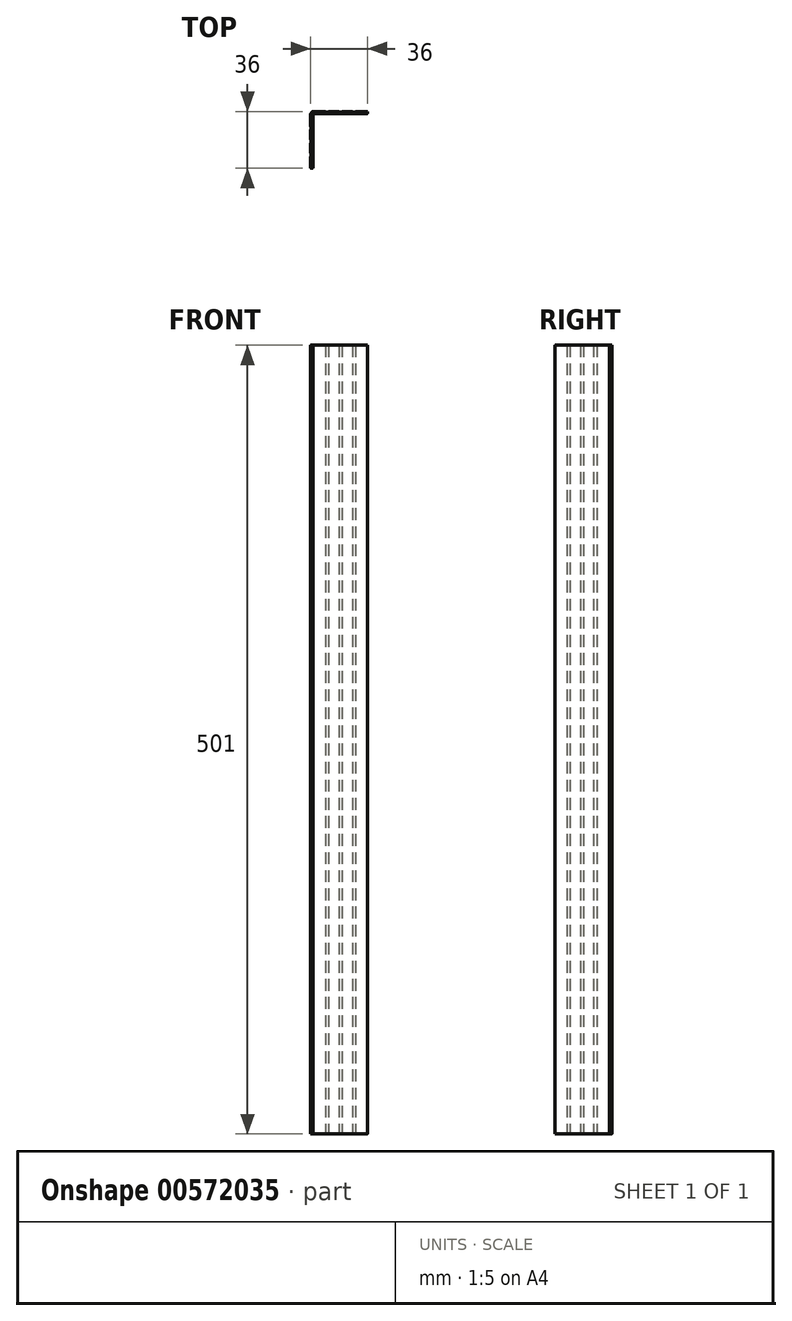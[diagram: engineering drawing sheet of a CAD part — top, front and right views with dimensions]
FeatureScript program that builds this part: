
annotation { "Feature Type Name" : "Feature", "Feature Type Description" : "" }
export const myFeature = defineFeature(function(context is Context, id is Id, definition is map)
    precondition{}
    {
        {
            var Q0;
            Q0=qCreatedBy(makeId("Top.planeOp"),FACE);
            var sketch = newSketch(context, id + "F0", { "sketchPlane" : qUnion([Q0])});
            skLineSegment(sketch, "E0", {"start": v(0, 0) * mm, "end": v(0, 7.5) * mm});
            skPoint(sketch, "E1.visualSharp", {"position": v(0, 36) * mm});
            skArc(sketch, "E1.filletArc", {"start": v(0.59, 35.41) * mm, "mid": v(0.15, 34.77) * mm, "end": v(0, 34) * mm});
            skLineSegment(sketch, "E2.1", {"start": v(1.5, 0) * mm, "end": v(1.5, 33.5) * mm});
            skLineSegment(sketch, "E3", {"start": v(1.5, 0) * mm, "end": v(0, 0) * mm});
            skPoint(sketch, "E4.visualSharp", {"position": v(1.5, 34.5) * mm});
            skArc(sketch, "E4.filletArc", {"start": v(1.8, 34.2) * mm, "mid": v(1.58, 33.88) * mm, "end": v(1.5, 33.5) * mm});
            skLineSegment(sketch, "E5.bottom", {"start": v(0, 18) * mm, "end": v(0.25, 18) * mm});
            skLineSegment(sketch, "E5.top", {"start": v(0, 16) * mm, "end": v(0.25, 16) * mm});
            skLineSegment(sketch, "E5.right", {"start": v(0.25, 18) * mm, "end": v(0.25, 16) * mm});
            skPoint(sketch, "E5.middle", {"position": v(0, 17) * mm});
            skLineSegment(sketch, "E6", {"start": v(0, 0) * mm, "end": v(-1.84, 0) * mm, "construction": true});
            skLineSegment(sketch, "E7", {"start": v(-1.84, 0) * mm, "end": v(-1.84, 17) * mm, "construction": true});
            skPoint(sketch, "E7.endSnap0", {"position": v(-0.25, 17) * mm});
            skLineSegment(sketch, "E8", {"start": v(-1.84, 8.5) * mm, "end": v(0, 8.5) * mm, "construction": true});
            skLineSegment(sketch, "E9.bottom", {"start": v(0.25, 9.5) * mm, "end": v(0, 9.5) * mm});
            skLineSegment(sketch, "E9.top", {"start": v(0.25, 7.5) * mm, "end": v(0, 7.5) * mm});
            skLineSegment(sketch, "E9.left", {"start": v(0.25, 9.5) * mm, "end": v(0.25, 7.5) * mm});
            skPoint(sketch, "E9.middle", {"position": v(0, 8.5) * mm});
            skLineSegment(sketch, "E10", {"start": v(-1.84, 17) * mm, "end": v(-1.84, 34) * mm, "construction": true});
            skLineSegment(sketch, "E11", {"start": v(-1.84, 25.5) * mm, "end": v(0, 25.5) * mm, "construction": true});
            skLineSegment(sketch, "E12.bottom", {"start": v(0.25, 26.5) * mm, "end": v(0, 26.5) * mm});
            skLineSegment(sketch, "E12.top", {"start": v(0.25, 24.5) * mm, "end": v(0, 24.5) * mm});
            skLineSegment(sketch, "E12.left", {"start": v(0.25, 26.5) * mm, "end": v(0.25, 24.5) * mm});
            skPoint(sketch, "E12.middle", {"position": v(0, 25.5) * mm});
            skPoint(sketch, "E13.end.orphan", {"position": v(36, 36) * mm});
            skLineSegment(sketch, "E14.trimOffspring", {"start": v(0, 9.5) * mm, "end": v(0, 16) * mm});
            skPoint(sketch, "E15.orphan", {"position": v(-0.25, 9.5) * mm});
            skPoint(sketch, "E16.orphan", {"position": v(-0.25, 7.5) * mm});
            skPoint(sketch, "E17.orphan", {"position": v(-0.25, 16) * mm});
            skLineSegment(sketch, "E18.trimOffspring", {"start": v(0, 18) * mm, "end": v(0, 24.5) * mm});
            skPoint(sketch, "E19.orphan", {"position": v(-0.25, 18) * mm});
            skLineSegment(sketch, "E20.trimOffspring", {"start": v(0, 26.5) * mm, "end": v(0, 34) * mm});
            skPoint(sketch, "E21.orphan", {"position": v(-0.25, 24.5) * mm});
            skPoint(sketch, "E22.orphan", {"position": v(-0.25, 26.5) * mm});
            skLineSegment(sketch, "E23.MirrorCS", {"start": v(11.5, 35.75) * mm, "end": v(11.5, 36) * mm});
            skLineSegment(sketch, "E24.MirrorCS", {"start": v(26.5, 35.75) * mm, "end": v(28.5, 35.75) * mm});
            skLineSegment(sketch, "E25.MirrorCS", {"start": v(28.5, 35.75) * mm, "end": v(28.5, 36) * mm});
            skLineSegment(sketch, "E26.MirrorCS", {"start": v(9.5, 35.75) * mm, "end": v(11.5, 35.75) * mm});
            skLineSegment(sketch, "E27.MirrorCS", {"start": v(9.5, 35.75) * mm, "end": v(9.5, 36) * mm});
            skLineSegment(sketch, "E28.MirrorCS", {"start": v(20, 36) * mm, "end": v(20, 35.75) * mm});
            skLineSegment(sketch, "E29.MirrorCS", {"start": v(26.5, 35.75) * mm, "end": v(26.5, 36) * mm});
            skLineSegment(sketch, "E30.MirrorCS", {"start": v(18, 35.75) * mm, "end": v(20, 35.75) * mm});
            skLineSegment(sketch, "E31.MirrorCS", {"start": v(18, 36) * mm, "end": v(18, 35.75) * mm});
            skArc(sketch, "E32.MirrorCS", {"start": v(1.8, 34.2) * mm, "mid": v(2.12, 34.42) * mm, "end": v(2.5, 34.5) * mm});
            skLineSegment(sketch, "E33.MirrorCS", {"start": v(36, 34.5) * mm, "end": v(36, 36) * mm});
            skArc(sketch, "E34.MirrorCS", {"start": v(0.59, 35.41) * mm, "mid": v(1.23, 35.85) * mm, "end": v(2, 36) * mm});
            skLineSegment(sketch, "E35.MirrorCS", {"start": v(10.5, 37.84) * mm, "end": v(10.5, 36) * mm, "construction": true});
            skLineSegment(sketch, "E36.MirrorCS", {"start": v(36, 36) * mm, "end": v(36, 37.84) * mm, "construction": true});
            skPoint(sketch, "E37.MirrorP", {"position": v(19, 36.25) * mm});
            skLineSegment(sketch, "E38.MirrorCS", {"start": v(27.5, 37.84) * mm, "end": v(27.5, 36) * mm, "construction": true});
            skPoint(sketch, "E39.MirrorP", {"position": v(19, 36) * mm});
            skLineSegment(sketch, "E40.MirrorCS", {"start": v(36, 34.5) * mm, "end": v(2.5, 34.5) * mm});
            skPoint(sketch, "E41.MirrorP", {"position": v(27.5, 36) * mm});
            skLineSegment(sketch, "E42.MirrorCS", {"start": v(36, 36) * mm, "end": v(28.5, 36) * mm});
            skLineSegment(sketch, "E43.MirrorCS", {"start": v(19, 37.84) * mm, "end": v(2, 37.84) * mm, "construction": true});
            skPoint(sketch, "E44.MirrorP", {"position": v(28.5, 36.25) * mm});
            skLineSegment(sketch, "E45.MirrorCS", {"start": v(18, 36) * mm, "end": v(11.5, 36) * mm});
            skPoint(sketch, "E46.MirrorP", {"position": v(18, 36.25) * mm});
            skPoint(sketch, "E47.MirrorP", {"position": v(10.5, 36) * mm});
            skPoint(sketch, "E48.MirrorP", {"position": v(9.5, 36.25) * mm});
            skPoint(sketch, "E49.MirrorP", {"position": v(20, 36.25) * mm});
            skPoint(sketch, "E50.MirrorP", {"position": v(26.5, 36.25) * mm});
            skLineSegment(sketch, "E51.MirrorCS", {"start": v(9.5, 36) * mm, "end": v(2, 36) * mm});
            skLineSegment(sketch, "E52.MirrorCS", {"start": v(36, 37.84) * mm, "end": v(19, 37.84) * mm, "construction": true});
            skPoint(sketch, "E53.MirrorP", {"position": v(11.5, 36.25) * mm});
            skLineSegment(sketch, "E54.MirrorCS", {"start": v(26.5, 36) * mm, "end": v(20, 36) * mm});
            skSolve(sketch);
        }
        {
            var Q0;
            Q0 = qSketchRegion(id + "F0", true);
            extrude(context, id + "F1", {"entities" : qUnion([Q0]), "depth" : 501 * mm, "offsetDistance" : 25 * mm});
        }
        {
            var Q0;
            Q0=makeQuery(id+"F1.opExtrude","SWEPT_EDGE",EDGE,{"disambiguationData":[OSD([sQuery(id+"F0.wireOp",EDGE,"E5.top"),sQuery(id+"F0.wireOp",EDGE,"E14.trimOffspring")])]});
            var Q1;
            Q1=makeQuery(id+"F1.opExtrude","SWEPT_EDGE",EDGE,{"disambiguationData":[OSD([sQuery(id+"F0.wireOp",EDGE,"E5.bottom"),sQuery(id+"F0.wireOp",EDGE,"E18.trimOffspring")])]});
            var Q2;
            Q2=makeQuery(id+"F1.opExtrude","SWEPT_EDGE",EDGE,{"disambiguationData":[OSD([sQuery(id+"F0.wireOp",EDGE,"E9.bottom"),sQuery(id+"F0.wireOp",EDGE,"E14.trimOffspring")])]});
            var Q3;
            Q3=makeQuery(id+"F1.opExtrude","SWEPT_EDGE",EDGE,{"disambiguationData":[OSD([sQuery(id+"F0.wireOp",EDGE,"E0"),sQuery(id+"F0.wireOp",EDGE,"E9.top")])]});
            var Q4;
            Q4=makeQuery(id+"F1.opExtrude","SWEPT_EDGE",EDGE,{"disambiguationData":[OSD([sQuery(id+"F0.wireOp",EDGE,"E12.bottom"),sQuery(id+"F0.wireOp",EDGE,"E20.trimOffspring")])]});
            var Q5;
            Q5=makeQuery(id+"F1.opExtrude","SWEPT_EDGE",EDGE,{"disambiguationData":[OSD([sQuery(id+"F0.wireOp",EDGE,"E12.top"),sQuery(id+"F0.wireOp",EDGE,"E18.trimOffspring")])]});
            var Q6;
            Q6=makeQuery(id+"F1.opExtrude","SWEPT_EDGE",EDGE,{"disambiguationData":[OSD([sQuery(id+"F0.wireOp",EDGE,"E27.MirrorCS"),sQuery(id+"F0.wireOp",EDGE,"E51.MirrorCS")])]});
            var Q7;
            Q7=makeQuery(id+"F1.opExtrude","SWEPT_EDGE",EDGE,{"disambiguationData":[OSD([sQuery(id+"F0.wireOp",EDGE,"E23.MirrorCS"),sQuery(id+"F0.wireOp",EDGE,"E45.MirrorCS")])]});
            var Q8;
            Q8=makeQuery(id+"F1.opExtrude","SWEPT_EDGE",EDGE,{"disambiguationData":[OSD([sQuery(id+"F0.wireOp",EDGE,"E31.MirrorCS"),sQuery(id+"F0.wireOp",EDGE,"E45.MirrorCS")])]});
            var Q9;
            Q9=makeQuery(id+"F1.opExtrude","SWEPT_EDGE",EDGE,{"disambiguationData":[OSD([sQuery(id+"F0.wireOp",EDGE,"E28.MirrorCS"),sQuery(id+"F0.wireOp",EDGE,"E54.MirrorCS")])]});
            var Q10;
            Q10=makeQuery(id+"F1.opExtrude","SWEPT_EDGE",EDGE,{"disambiguationData":[OSD([sQuery(id+"F0.wireOp",EDGE,"E29.MirrorCS"),sQuery(id+"F0.wireOp",EDGE,"E54.MirrorCS")])]});
            var Q11;
            Q11=makeQuery(id+"F1.opExtrude","SWEPT_EDGE",EDGE,{"disambiguationData":[OSD([sQuery(id+"F0.wireOp",EDGE,"E25.MirrorCS"),sQuery(id+"F0.wireOp",EDGE,"E42.MirrorCS")])]});
            var Q12;
            Q12=makeQuery(id+"F1.opExtrude","SWEPT_EDGE",EDGE,{"disambiguationData":[OSD([sQuery(id+"F0.wireOp",EDGE,"E33.MirrorCS"),sQuery(id+"F0.wireOp",EDGE,"E42.MirrorCS")])]});
            var Q13;
            Q13=makeQuery(id+"F1.opExtrude","SWEPT_EDGE",EDGE,{"disambiguationData":[OSD([sQuery(id+"F0.wireOp",EDGE,"E33.MirrorCS"),sQuery(id+"F0.wireOp",EDGE,"E40.MirrorCS")])]});
            var Q14;
            Q14=makeQuery(id+"F1.opExtrude","SWEPT_EDGE",EDGE,{"disambiguationData":[OSD([sQuery(id+"F0.wireOp",EDGE,"E0"),sQuery(id+"F0.wireOp",EDGE,"E3")])]});
            var Q15;
            Q15=makeQuery(id+"F1.opExtrude","SWEPT_EDGE",EDGE,{"disambiguationData":[OSD([sQuery(id+"F0.wireOp",EDGE,"E2.1"),sQuery(id+"F0.wireOp",EDGE,"E3")])]});
            fillet(context, id + "F2", {"entities" : qUnion([Q0, Q1, Q2, Q3, Q4, Q5, Q6, Q7, Q8, Q9, Q10, Q11, Q12, Q13, Q14, Q15]), "radius" : 0.2 * mm, "tangentPropagation" : true, "allowEdgeOverflow" : false});
        }
    });
